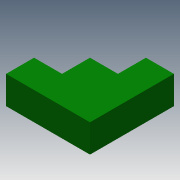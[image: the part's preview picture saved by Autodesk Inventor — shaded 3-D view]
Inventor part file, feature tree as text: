
AUTODESK INVENTOR PART (.ipt)
format: ipt  version: 2015 (Build 190159000, 159)  size: 117,760 bytes
history: native  units: in
note: dims shown in document units (in); Inventor stores cm internally (conversion verified against a paired STEP export)
features: extrude x1, sketch x1
ambient origin geometry x8: Origin, YZ Plane, XZ Plane, XY Plane, X Axis, Y Axis, Z Axis, Center Point
bodies: Solid1 (feature_tree)
feature tree (2):
  extrude  "Extrusion1"  Depth=1.0in
  sketch  "Sketch1"  dims[d0=3.0in d1=1.0in d2=1.0in d3=1.0in d4=1.0in d5=1.0in d6=1.0in d7=0.0in]
